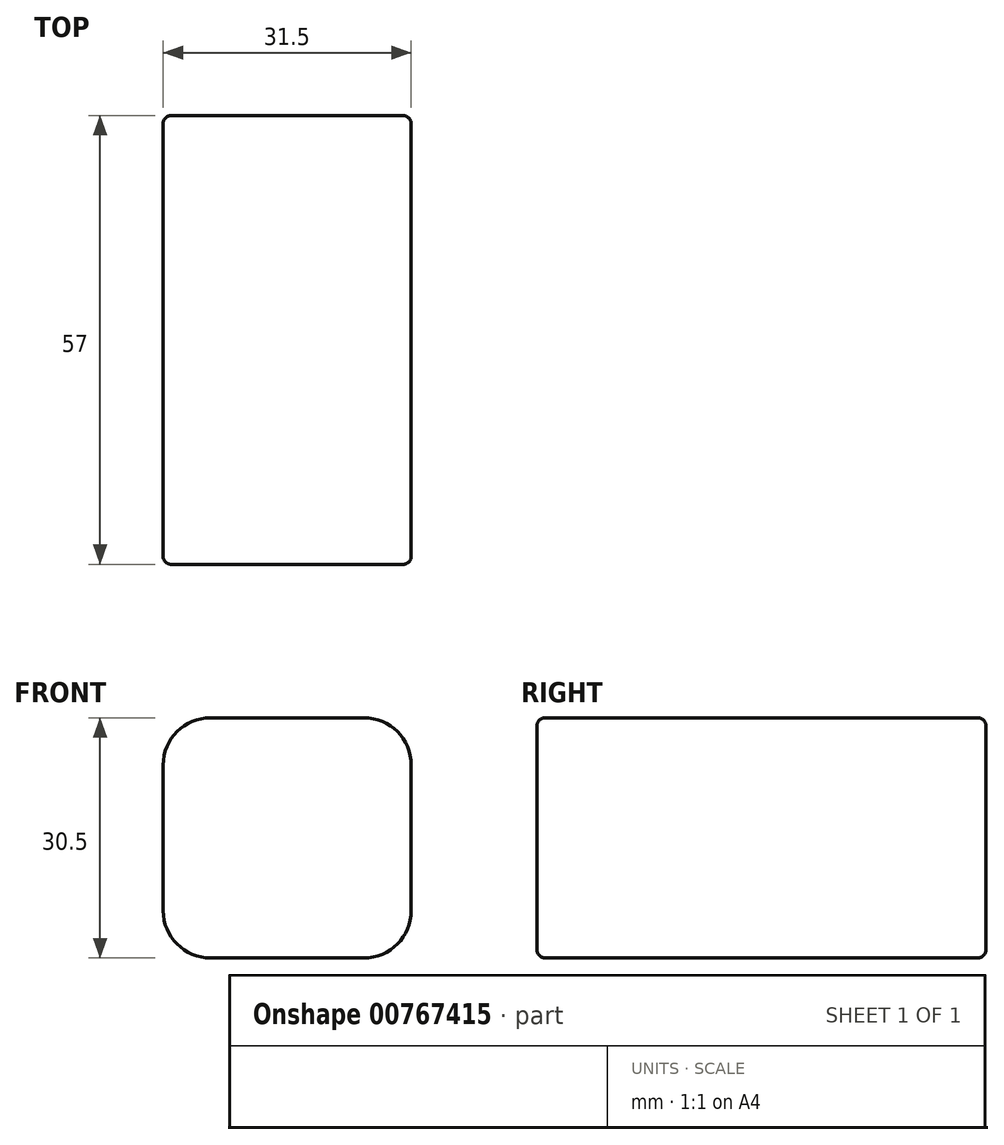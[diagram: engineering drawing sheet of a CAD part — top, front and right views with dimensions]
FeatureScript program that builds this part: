
annotation { "Feature Type Name" : "Feature", "Feature Type Description" : "" }
export const myFeature = defineFeature(function(context is Context, id is Id, definition is map)
    precondition{}
    {
        {
            var Q0;
            Q0=qCreatedBy(makeId("Front.planeOp"),FACE);
            var sketch = newSketch(context, id + "F0", { "sketchPlane" : qUnion([Q0])});
            skLineSegment(sketch, "E0", {"start": v(-15.75, 0) * mm, "end": v(-15.75, 9.25) * mm});
            skLineSegment(sketch, "E1", {"start": v(-9.75, 15.25) * mm, "end": v(0, 15.25) * mm});
            skLineSegment(sketch, "E2", {"start": v(-15.75, 0) * mm, "end": v(-15.75, -9.25) * mm});
            skLineSegment(sketch, "E3", {"start": v(-9.75, -15.25) * mm, "end": v(0, -15.25) * mm});
            skLineSegment(sketch, "E4.MirrorCS", {"start": v(9.75, 15.25) * mm, "end": v(0, 15.25) * mm});
            skLineSegment(sketch, "E5.MirrorCS", {"start": v(9.75, -15.25) * mm, "end": v(0, -15.25) * mm});
            skLineSegment(sketch, "E6.MirrorCS", {"start": v(15.75, 0) * mm, "end": v(15.75, 9.25) * mm});
            skLineSegment(sketch, "E7.MirrorCS", {"start": v(15.75, 0) * mm, "end": v(15.75, -9.25) * mm});
            skPoint(sketch, "E8.visualSharp", {"position": v(-15.75, 15.25) * mm});
            skArc(sketch, "E8.filletArc", {"start": v(-9.75, 15.25) * mm, "mid": v(-14, 13.5) * mm, "end": v(-15.75, 9.25) * mm});
            skPoint(sketch, "E9.visualSharp", {"position": v(15.75, 15.25) * mm});
            skArc(sketch, "E9.filletArc", {"start": v(15.75, 9.25) * mm, "mid": v(14, 13.5) * mm, "end": v(9.75, 15.25) * mm});
            skPoint(sketch, "E10.visualSharp", {"position": v(15.75, -15.25) * mm});
            skArc(sketch, "E10.filletArc", {"start": v(9.75, -15.25) * mm, "mid": v(14, -13.5) * mm, "end": v(15.75, -9.25) * mm});
            skPoint(sketch, "E11.visualSharp", {"position": v(-15.75, -15.25) * mm});
            skArc(sketch, "E11.filletArc", {"start": v(-15.75, -9.25) * mm, "mid": v(-14, -13.5) * mm, "end": v(-9.75, -15.25) * mm});
            skSolve(sketch);
        }
        {
            var Q0;
            Q0 = qSketchRegion(id + "F0", true);
            extrude(context, id + "F1", {"entities" : qUnion([Q0]), "oppositeDirection" : true, "depth" : 57 * mm, "offsetDistance" : 25 * mm});
        }
        {
            var Q0;
            Q0=makeQuery(id+"F1.opExtrude","CAP_EDGE",EDGE,{"disambiguationData":[OSD([sQuery(id+"F0.wireOp",EDGE,"E1"),sQuery(id+"F0.wireOp",EDGE,"E4.MirrorCS")])],"isStart":true});
            var Q1;
            Q1=makeQuery(id+"F1.opExtrude","CAP_EDGE",EDGE,{"disambiguationData":[OSD([sQuery(id+"F0.wireOp",EDGE,"E1"),sQuery(id+"F0.wireOp",EDGE,"E4.MirrorCS")])],"isStart":false});
            fillet(context, id + "F2", {"entities" : qUnion([Q0, Q1]), "radius" : 1 * mm, "tangentPropagation" : true, "allowEdgeOverflow" : false});
        }
    });
